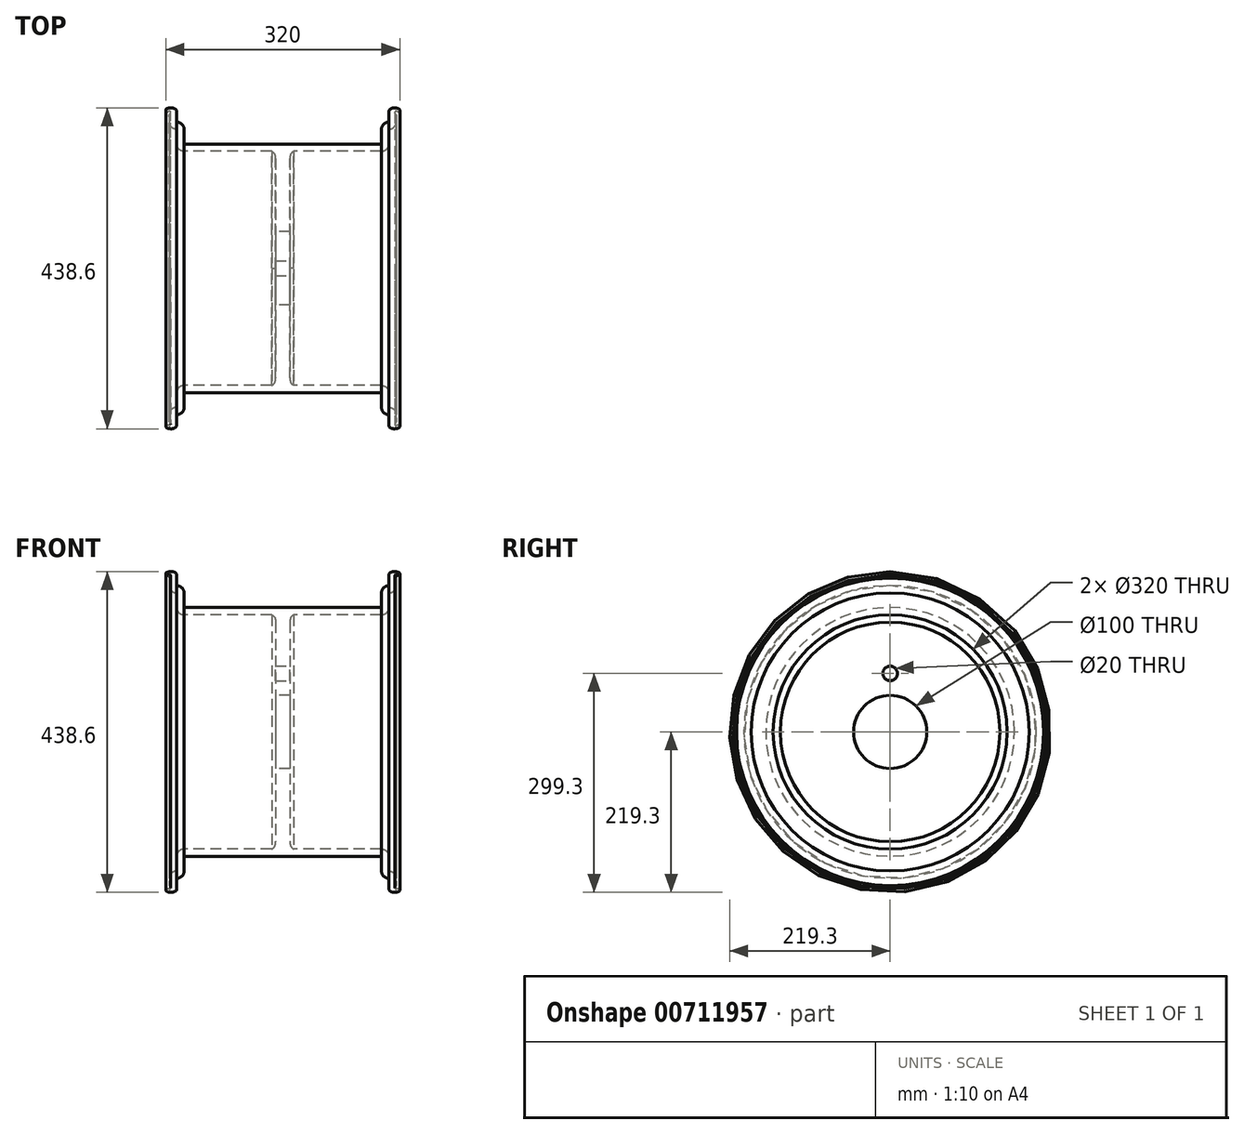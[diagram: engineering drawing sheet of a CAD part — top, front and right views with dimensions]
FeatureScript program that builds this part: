
annotation { "Feature Type Name" : "Feature", "Feature Type Description" : "" }
export const myFeature = defineFeature(function(context is Context, id is Id, definition is map)
    precondition{}
    {
        {
            var Q0;
            Q0=qCreatedBy(makeId("Front.planeOp"),FACE);
            var sketch = newSketch(context, id + "F0", { "sketchPlane" : qUnion([Q0])});
            skLineSegment(sketch, "E0", {"start": v(-15, 160) * mm, "end": v(-135, 160) * mm});
            skLineSegment(sketch, "E1", {"start": v(-145, 170) * mm, "end": v(-145, 190) * mm});
            skLineSegment(sketch, "E2", {"start": v(-145, 190) * mm, "end": v(-145, 190) * mm});
            skLineSegment(sketch, "E3", {"start": v(-155, 210) * mm, "end": v(-155, 200) * mm});
            skPoint(sketch, "E4.visualSharp", {"position": v(-155, 190) * mm});
            skArc(sketch, "E4.filletArc", {"start": v(-155, 200) * mm, "mid": v(-152.07, 192.93) * mm, "end": v(-145, 190) * mm});
            skPoint(sketch, "E5.visualSharp", {"position": v(-145, 160) * mm});
            skArc(sketch, "E5.filletArc", {"start": v(-145, 170) * mm, "mid": v(-142.07, 162.93) * mm, "end": v(-135, 160) * mm});
            skFitSpline(sketch, "E6", {"points": [v(-15, 160) * mm, v(-10, 150) * mm], "startDerivative": vector(15.8, -7.87) * mm, "endDerivative": vector(0.2, -10.42) * mm});
            skLineSegment(sketch, "E7", {"start": v(-135, 170) * mm, "end": v(-135, 190) * mm});
            skLineSegment(sketch, "E8.0", {"start": v(-145, 210) * mm, "end": v(-145, 200) * mm});
            skFitSpline(sketch, "E9", {"points": [v(-145, 200) * mm, v(-135, 190) * mm], "startDerivative": vector(12.67, 0.4) * mm, "endDerivative": vector(-0.49, -19.1) * mm});
            skFitSpline(sketch, "E10", {"points": [v(-155, 210) * mm, v(-153.28, 213.41) * mm, v(-155, 215) * mm, v(-157.5, 213.7) * mm, v(-160, 216.45) * mm, v(-155.5, 219.05) * mm, v(-148.85, 218.66) * mm, v(-145.38, 215.82) * mm, v(-145, 210) * mm], "startDerivative": vector(22.55, 28.44) * mm, "endDerivative": vector(-2.88, -42.48) * mm});
            skLineSegment(sketch, "E11.MirrorCS", {"start": v(145, 210) * mm, "end": v(145, 200) * mm});
            skFitSpline(sketch, "E12.MirrorCS", {"points": [v(15, 160) * mm, v(10, 150) * mm], "startDerivative": vector(-15.8, -7.87) * mm, "endDerivative": vector(-0.2, -10.42) * mm});
            skFitSpline(sketch, "E13.MirrorCS", {"points": [v(145, 200) * mm, v(135, 190) * mm], "startDerivative": vector(-12.67, 0.4) * mm, "endDerivative": vector(0.49, -19.1) * mm});
            skLineSegment(sketch, "E14.MirrorCS", {"start": v(155, 210) * mm, "end": v(155, 200) * mm});
            skFitSpline(sketch, "E15.MirrorCS", {"points": [v(155, 210) * mm, v(153.28, 213.41) * mm, v(155, 215) * mm, v(157.5, 213.7) * mm, v(160, 216.45) * mm, v(155.5, 219.05) * mm, v(148.85, 218.66) * mm, v(145.38, 215.82) * mm, v(145, 210) * mm], "startDerivative": vector(-22.55, 28.44) * mm, "endDerivative": vector(2.88, -42.48) * mm});
            skArc(sketch, "E16.MirrorCS", {"start": v(155, 200) * mm, "mid": v(152.07, 192.93) * mm, "end": v(145, 190) * mm});
            skArc(sketch, "E17.MirrorCS", {"start": v(145, 170) * mm, "mid": v(142.07, 162.93) * mm, "end": v(135, 160) * mm});
            skPoint(sketch, "E18.MirrorP", {"position": v(145, 160) * mm});
            skLineSegment(sketch, "E19.MirrorCS", {"start": v(135, 170) * mm, "end": v(135, 190) * mm});
            skLineSegment(sketch, "E20.MirrorCS", {"start": v(145, 170) * mm, "end": v(145, 190) * mm});
            skLineSegment(sketch, "E21.MirrorCS", {"start": v(15, 160) * mm, "end": v(135, 160) * mm});
            skPoint(sketch, "E22.MirrorP", {"position": v(155, 190) * mm});
            skLineSegment(sketch, "E23", {"start": v(-10, 150) * mm, "end": v(-10, 50) * mm});
            skLineSegment(sketch, "E24", {"start": v(-135, 170) * mm, "end": v(135, 170) * mm});
            skLineSegment(sketch, "E25", {"start": v(-10, 50) * mm, "end": v(10, 50) * mm});
            skLineSegment(sketch, "E26", {"start": v(10, 50) * mm, "end": v(10, 150) * mm});
            skLineSegment(sketch, "E27", {"start": v(-190.26, 0) * mm, "end": v(183.03, 0) * mm, "construction": true});
            skSolve(sketch);
        }
        {
            var Q0;
            Q0 = qSketchRegion(id + "F0", true);
            var Q1;
            Q1=sQuery(id+"F0.wireOp",EDGE,"E27");
            revolve(context, id + "F1", {"surfaceOperationType" : NewSurfaceOperationType.NEW, "entities" : qUnion([Q0]), "axis" : qUnion([Q1]), "revolveType" : RevolveType.FULL});
        }
        {
            var Q0;
            Q0=makeQuery(id+"F1.opRevolve","SWEPT_FACE",FACE,{"disambiguationData":[OSD([sQuery(id+"F0.wireOp",EDGE,"E26")])]});
            var sketch = newSketch(context, id + "F2", { "sketchPlane" : qUnion([Q0])});
            skCircle(sketch, "E28", {"center": v(0, 80) * mm, "radius": 10 * mm});
            skSolve(sketch);
        }
        {
            var Q0;
            Q0=makeQuery(id+"F2.imprint","IMPRINT",FACE,{"disambiguationData":[TD([[makeQuery(id+"F2.imprint","IMPRINT",EDGE,{"derivedFrom":sQuery(id+"F2.wireOp",EDGE,"E28")}),1.0]])]});
            var Q1;
            Q1=sQuery(id+"F2.wireOp",EDGE,"E28");
            extrude(context, id + "F3", {"entities" : qUnion([Q0]), "operationType" : NewBodyOperationType.REMOVE, "surfaceEntities" : qUnion([Q1]), "oppositeDirection" : true, "depth" : 20 * mm, "offsetDistance" : 25 * mm});
        }
        {
            var Q0;
            Q0=makeQuery(id+"F1.opRevolve","SWEPT_BODY",BODY,{"disambiguationData":[OSD([sQuery(id+"F0.wireOp",EDGE,"E0"),sQuery(id+"F0.wireOp",EDGE,"E1"),sQuery(id+"F0.wireOp",EDGE,"E3"),sQuery(id+"F0.wireOp",EDGE,"E4.filletArc"),sQuery(id+"F0.wireOp",EDGE,"E5.filletArc"),sQuery(id+"F0.wireOp",EDGE,"E6"),sQuery(id+"F0.wireOp",EDGE,"E7"),sQuery(id+"F0.wireOp",EDGE,"E8.0"),sQuery(id+"F0.wireOp",EDGE,"E9"),sQuery(id+"F0.wireOp",EDGE,"E10"),sQuery(id+"F0.wireOp",EDGE,"E11.MirrorCS"),sQuery(id+"F0.wireOp",EDGE,"E12.MirrorCS"),sQuery(id+"F0.wireOp",EDGE,"E13.MirrorCS"),sQuery(id+"F0.wireOp",EDGE,"E14.MirrorCS"),sQuery(id+"F0.wireOp",EDGE,"E15.MirrorCS"),sQuery(id+"F0.wireOp",EDGE,"E16.MirrorCS"),sQuery(id+"F0.wireOp",EDGE,"E17.MirrorCS"),sQuery(id+"F0.wireOp",EDGE,"E19.MirrorCS"),sQuery(id+"F0.wireOp",EDGE,"E20.MirrorCS"),sQuery(id+"F0.wireOp",EDGE,"E21.MirrorCS"),sQuery(id+"F0.wireOp",EDGE,"E23"),sQuery(id+"F0.wireOp",EDGE,"E24"),sQuery(id+"F0.wireOp",EDGE,"E25"),sQuery(id+"F0.wireOp",EDGE,"E26")])]});
            var Q1;
            Q1=sQuery(id+"F0.wireOp",EDGE,"E27");
            circularPattern(context, id + "F4", {"operationType" : NewBodyOperationType.ADD, "entities" : qUnion([Q0]), "axis" : qUnion([Q1]), "angle" : 360 * degree, "instanceCount" : 6, "oppositeDirection" : true});
        }
    });
